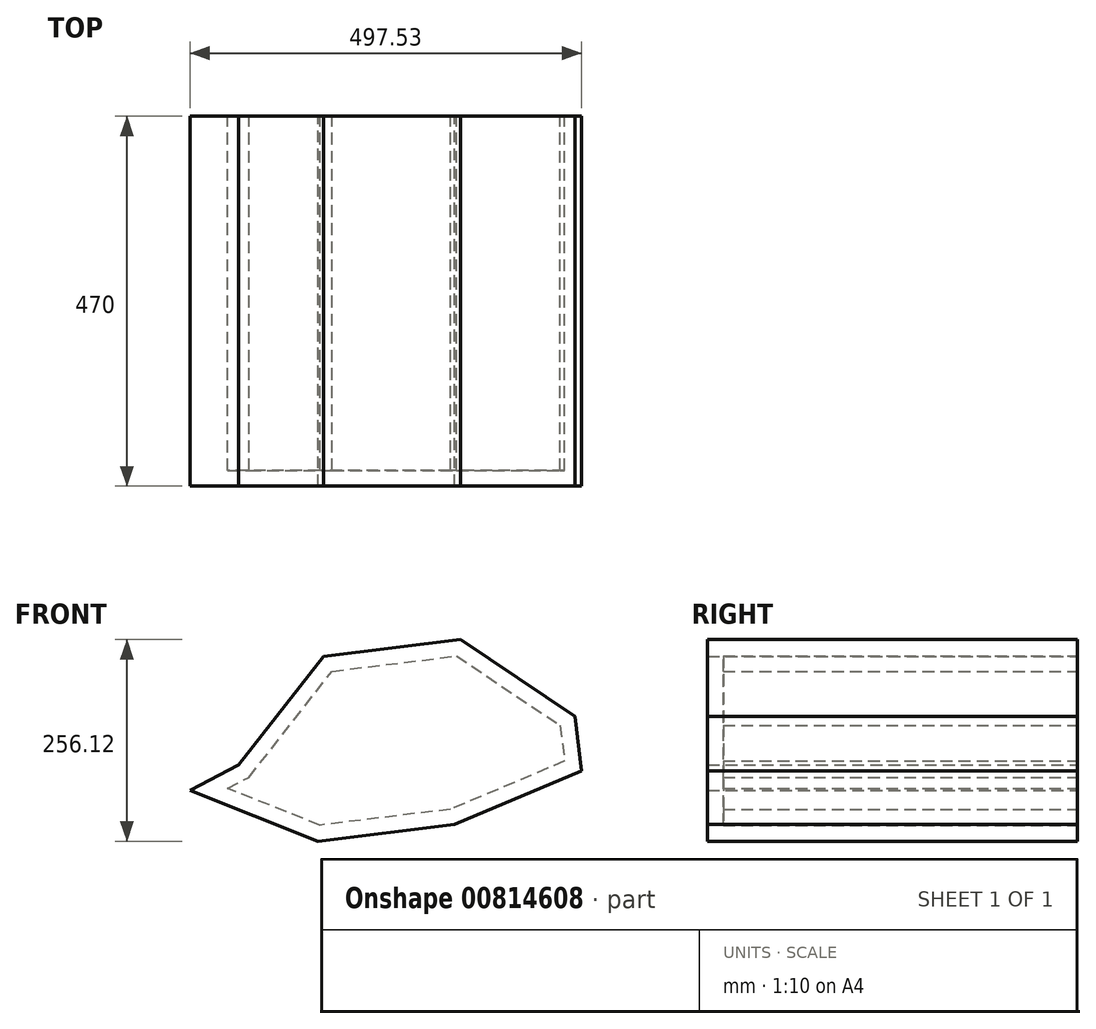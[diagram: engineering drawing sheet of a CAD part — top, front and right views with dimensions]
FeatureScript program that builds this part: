
annotation { "Feature Type Name" : "Feature", "Feature Type Description" : "" }
export const myFeature = defineFeature(function(context is Context, id is Id, definition is map)
    precondition{}
    {
        {
            var Q0;
            Q0=qCreatedBy(makeId("Front.planeOp"),FACE);
            var sketch = newSketch(context, id + "F0", { "sketchPlane" : qUnion([Q0])});
            skLineSegment(sketch, "E0.0", {"start": v(179.23, 197.42) * mm, "end": v(324.7, 100.15) * mm});
            skLineSegment(sketch, "E0.1", {"start": v(324.7, 100.15) * mm, "end": v(333.2, 30.66) * mm});
            skLineSegment(sketch, "E0.2", {"start": v(333.2, 30.66) * mm, "end": v(172, -37.47) * mm});
            skLineSegment(sketch, "E0.3", {"start": v(172, -37.47) * mm, "end": v(-1.7, -58.7) * mm});
            skLineSegment(sketch, "E0.4", {"start": v(-1.7, -58.7) * mm, "end": v(-164.33, 5.93) * mm});
            skLineSegment(sketch, "E0.5", {"start": v(-164.33, 5.93) * mm, "end": v(-102.3, 38.35) * mm});
            skLineSegment(sketch, "E0.6", {"start": v(-102.3, 38.35) * mm, "end": v(5.53, 176.2) * mm});
            skLineSegment(sketch, "E0.7", {"start": v(5.53, 176.2) * mm, "end": v(179.23, 197.42) * mm});
            skPoint(sketch, "E0.0.midPoint", {"position": v(251.97, 148.79) * mm});
            skSolve(sketch);
        }
        {
            var Q0;
            Q0=makeQuery(id+"F0.imprint","IMPRINT",FACE,{"disambiguationData":[TD([[makeQuery(id+"F0.imprint","IMPRINT",EDGE,{"derivedFrom":sQuery(id+"F0.wireOp",EDGE,"E0.0")}),-1.0]])]});
            extrude(context, id + "F1", {"entities" : qUnion([Q0]), "depth" : 470 * mm, "offsetDistance" : 25 * mm});
        }
        {
            var Q0;
            Q0=makeQuery(id+"F1.opExtrude","CAP_FACE",FACE,{"disambiguationData":[OSD([sQuery(id+"F0.wireOp",EDGE,"E0.0"),sQuery(id+"F0.wireOp",EDGE,"E0.1"),sQuery(id+"F0.wireOp",EDGE,"E0.2"),sQuery(id+"F0.wireOp",EDGE,"E0.3"),sQuery(id+"F0.wireOp",EDGE,"E0.4"),sQuery(id+"F0.wireOp",EDGE,"E0.5"),sQuery(id+"F0.wireOp",EDGE,"E0.6"),sQuery(id+"F0.wireOp",EDGE,"E0.7")])],"isStart":true});
            shell(context, id + "F2", {"entities" : qUnion([Q0]), "thickness" : 20 * mm});
        }
    });
